# Revit family: Faucet-Lavatory-Spout-KOHLER-COMPONENTS-K-77968T
name_source: partatom
category: Plumbing Fixtures
revit_build: Autodesk Revit 2017 (Build: 20160225_1515(x64)
units: mm (PartAtom-declared; Revit-internal decimal feet)

## family parameters
Cut with Voids When Loaded = No
Host = Face
OmniClass Number = 23.31.11.00
OmniClass Title = Faucets
Part Type = Normal
Room Calculation Point = No
Round Connector Dimension = Use Diameter
Shared = No

## types (13) — shared parameters
ADA Compliant = No
Assembly Code = D2010
CW Connection = No
Cold Water Inlet = Cold Water Inlet
Date Modified = 01/15/2021
Default Elevation = 36"
Description = Yi Ting 8-inch basin faucet curve spout
Flow Rate = 0 GPM
HW Connection = No
Height = 10 3/8"
Hot Water Inlet = Hot Water Inlet
Length = 6 5/16"
Manufacturer = KOHLER Co.
Master Format 2014 = 22 41 39
Master Format 2014 Name = Residential Faucets, Supplies, and Trim
Material = Metal construction
Pressure = 0.00 psi
Product Name = COMPONENTS
Spout Reach = 6 5/16"
URL = http://www.kohler.com.cn
Vent Connection = No
Waste Connection = No
Waste Water Outlet = Waste Water Outlet
WaterSense Certified = No
Width = 2 3/8"

## per-type parameters (varying)
| type | Drain Included | Finish | Model | Product Documentation Link | Product Page URL | Type |
| AF- Flange Gold | Yes | Kohler-Metal-AF-Flange_Gold | K-77968T-AF | https://files.kohler.com.cn | https://www.kohler.com.cn | 1 |
| BN- Roman Silver | Yes | Kohler-Metal-BN-Roman_Silver | K-77968T-BN | https://files.kohler.com.cn | https://www.kohler.com.cn | 2 |
| RGD- Rose Gold | Yes | Kohler-Metal-RGD-Rose_Gold | K-77968T-RGD | https://files.kohler.com.cn | https://www.kohler.com.cn | 3 |
| CP- Polished Chrome | Yes | Kohler-Metal-CP-Polished_Chrome | K-77968T-CP | https://files.kohler.com.cn | https://www.kohler.com.cn | 4 |
| TT- Titanium Silver | Yes | Kohler-Metal-TT-Titanium_Silver | K-77968T-TT | https://files.kohler.com.cn | https://www.kohler.com.cn | 5 |
| 2BL- Original Black | Yes | Kohler-Metal-2BL-Original_Black | K-77968T-2BL | https://files.kohler.com.cn | https://www.kohler.com.cn | 6 |
| Without Drain,AF- Flange Gold | No | Kohler-Metal-AF-Flange_Gold | K-77968T-ND-AF |  |  | 8 |
| Without drain, BN- Roman Silver | No | Kohler-Metal-BN-Roman_Silver | K-77968T-ND-BN |  |  | 9 |
| Without drain, RGD- Rose Gold | No | Kohler-Metal-RGD-Rose_Gold | K-77968T-ND-RGD |  |  | 10 |
| Without drain, CP- Polished Chrome | No | Kohler-Metal-CP-Polished_Chrome | K-77968T-ND-CP |  |  | 11 |
| Without Drain, TT- Titanium Silver | No | Kohler-Metal-TT-Titanium_Silver | K-77968T-ND-TT |  |  | 12 |
| Without drain, 2BL- Original Black | No | Kohler-Metal-2BL-Original_Black | K-77968T-ND-2BL |  |  | 13 |
| MU(Limited Edition), BL- Matte Black | Yes | Kohler-Metal-BL-Matte_Black | K-77968T-MU-BL | https://files.kohler.com.cn | https://www.kohler.com.cn | 7 |

## geometry (parser evidence)
native form markers: Sweep x5
no freeform markers — native parametric forms only
